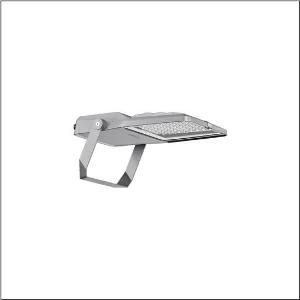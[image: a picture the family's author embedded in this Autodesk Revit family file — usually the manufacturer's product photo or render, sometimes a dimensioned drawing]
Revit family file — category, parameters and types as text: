
# Revit family: floodlight_fl_21_iq_mini___pl33t_5xa7772b1f1a_dd0a
name_source: partatom
category: Lighting Fixtures
units: mm (PartAtom-declared; Revit-internal decimal feet)

## family parameters
Cut with Voids When Loaded = No
Host = Face
Light Source = No
Part Type = Normal
Room Calculation Point = No
Round Connector Dimension = Use Diameter
Shared = No

## types (1)
- --- (1 x LED, 5110 lm, 45.5 W, 2200K)
    Apparent Load = 46 VA
    CIE Flux Codes = 26 75 99 100 100
    Color Rendering = 70
    Color Temperature = 2200K
    Default Elevation = 1800 mm
    Description = Floodlight FL 21 iQ mini, floodlight, primary light control with lens, of PMMA, primary optical cover: protective disc, of toughened safety glass, transparent, light distribution: PL33T, light emission: direct distribution, installation type: surface-mounted, LED, High Power LED, rated luminous flux: 5.110lm, luminous efficacy: 112lm/W, light colour: 722, colour temperature: 2200K, control: Street-Remote, Auto-Match, Temp-Guard, Night-Set, Smart-Wire, Desk-Remote (wireless, voltage-free reading and setting of iQ features in the workshop via application-optimized NFC function/RFID function), optimised constant luminous flux control (CLO 2.0), with terminal, 6-pole, mains connection: 220..240V, AC, 50/60Hz, start of lifetime: 46W, end of service life: 48W, reduction: 21W, luminaire housing, of diecast aluminium, powder-coated, Siteco® metallic grey (DB 702S), corrosivity category C5 mid according to DIN EN ISO 12944, sealing non-destructively replaceable, mounting bracket, of steel, galvanised, powder-coated, Siteco® metallic grey (DB 702S), protection rating (complete): IP66, insulation class (complete): insulation class II (safety insulation), certification: CE, ENEC, VDE, protection symbol: D, impact resistance: IK08, permissible operating ambient temperature: -40..+40°C, permissible operating ambient temperature for outdoor applications: -40..+50°C, standard: DIN EN 12944, LABS conformity tested according to VDMA 24364:2018-05, packaging unit: 1 piece

Light Distribution: PL33T
    Height = 70 mm
    Lamp = 1 x LED
    Lamp Light Flux = 5110 lm
    Lamp Power = 45.5 W
    Lamp count = 1
    Length = 485 mm
    Luminous efficacy = 112 lm/W
    Manufacturer = Siteco
    ModVariant = No
    Model = 5XA7772B1F1A
    Number of Poles = 1
    OnlyDefault = Yes
    Power Factor = 1
    Product Name = Floodlight FL 21 iQ mini | PL33T
    Product group = floodlight | pylon annexe
    ProductGroupID = 6200
    Protection Class = Protection class II
    Protection Degree = IP 66
    RLX_Detail_Level = 1
    RLX_Emergency_Light_Flux = 0 lm
    RLX_Emergency_Type = 0
    RLX_Emergency_Type_DB = No
    RlxData = <blob elided: 96009 chars, md5=b3a1ce46>
    Socket = socket
    Standby Power = 0 W
    System Light Flux = 5110 lm
    System Power = 46 W
    Type Comments = factory setting: luminous flux: 100 % | dim-lin: 254 | 463 mA
    Type Image = l_1006845.jpg
    URL = http://relux.com
    VarID = @adj_100297
    Voltage = 0 V
    Weight = 0.00 kg
    Width = 337 mm

## geometry (parser evidence)
native form markers: Blend x4, Sweep x12
no freeform markers — native parametric forms only
